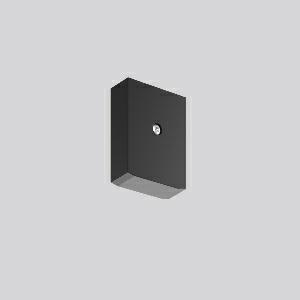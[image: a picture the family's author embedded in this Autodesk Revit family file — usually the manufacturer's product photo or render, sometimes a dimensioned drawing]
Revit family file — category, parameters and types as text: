
# Revit family: linedo_endkappe_b_f_982700_003_e18c
name_source: partatom
category: Lighting Fixtures
units: mm (PartAtom-declared; Revit-internal decimal feet)

## family parameters
Cut with Voids When Loaded = No
Host = Face
Light Source = No
Part Type = Normal
Room Calculation Point = No
Round Connector Dimension = Use Diameter
Shared = No

## types (1)
- LINEDO_Endkappe_B_F
    Apparent Load = 0 VA
    Default Elevation = 1800 mm
    Description = End cap low profile for LINEDO plug. Plastic end cap to cover the LINEDO plug system at the end of the line. Fastening by TX20 screw. Installation accessories included.
Colour: black
Length: 23 mm
Width: 58 mm
Height: 76 mm
Weight: 31 g
    Height = 76 mm
    Lamp = 0 x
    Length = 23 mm
    Luminous efficacy = 0 lm/W
    Manufacturer = RZB
    ModVariant = No
    Model = 982700.003
    Mounting Place = Ceiling
    Mounting Type = Pendant, Surface mounted
    Number of Poles = 1
    OnlyDefault = Yes
    Power Factor = 1
    Product Name = LINEDO_Endkappe_B_F
    Product group = Surface mounted continuous line luminaire system
    ProductGroupID = 310
    Protection Class = Protection class
    Protection Degree = Degree of protection
    RLX_Detail_Level = 1
    RLX_Emergency_Light_Flux = 0 lm
    RLX_Emergency_Type = 0
    RLX_Emergency_Type_DB = No
    RlxData = <blob elided: 10353 chars, md5=8d62d562>
    Standby Power = 0 W
    System Light Flux = 0 lm
    System Power = 0 W
    Type Comments = Product without accessories
    Type Image = 982700.003.jpg
    URL = http://relux.com
    VarID = ---
    Voltage = 0 V
    Weight = 0.00 kg
    Width = 58 mm

## geometry (parser evidence)
native form markers: Sweep x9
no freeform markers — native parametric forms only
